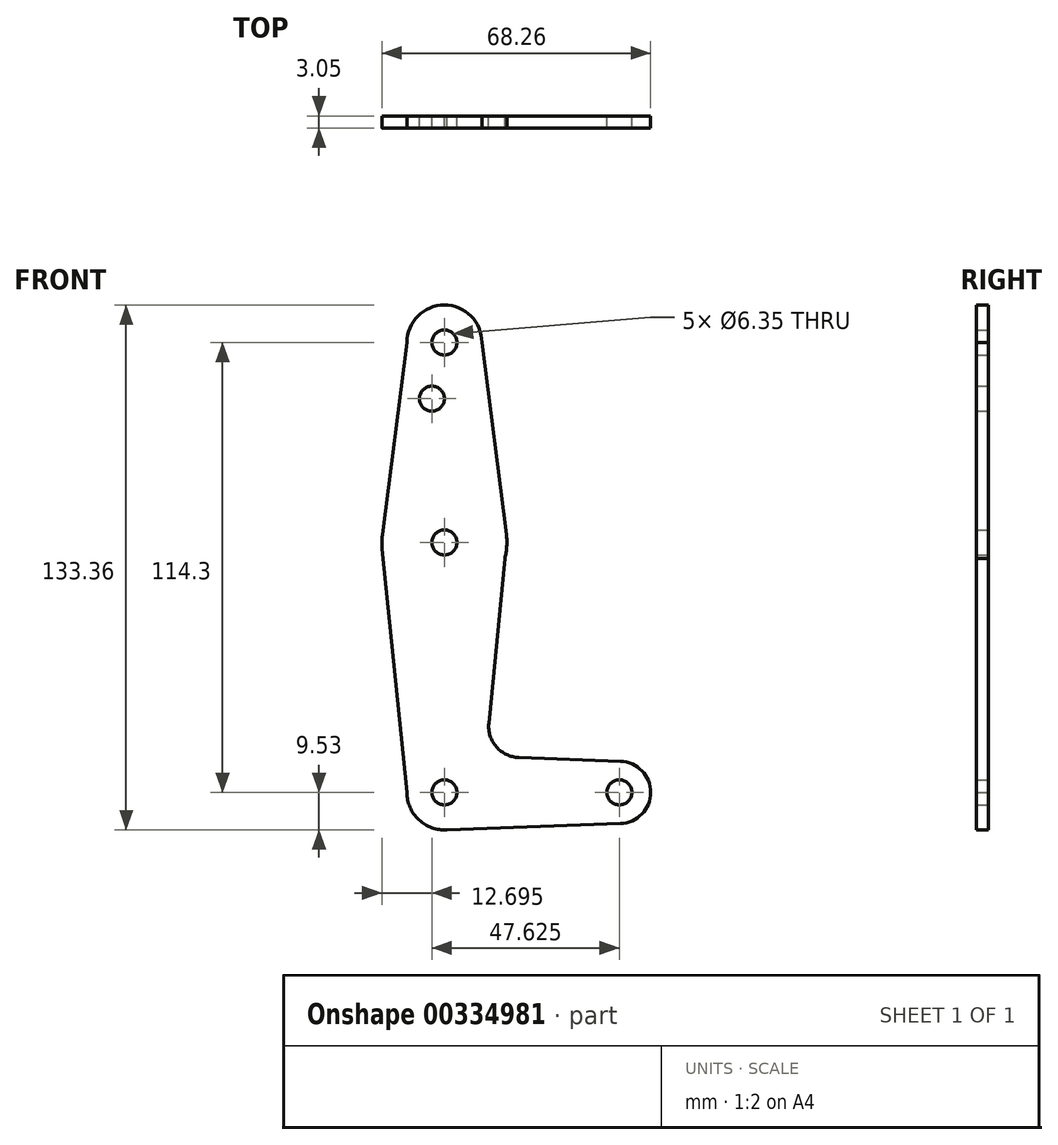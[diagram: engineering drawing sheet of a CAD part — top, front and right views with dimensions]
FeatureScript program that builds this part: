
annotation { "Feature Type Name" : "Feature", "Feature Type Description" : "" }
export const myFeature = defineFeature(function(context is Context, id is Id, definition is map)
    precondition{}
    {
        {
            var Q0;
            Q0=qCreatedBy(makeId("Front.planeOp"),FACE);
            var sketch = newSketch(context, id + "F0", { "sketchPlane" : qUnion([Q0])});
            skLineSegment(sketch, "E0", {"start": v(0, 0) * mm, "end": v(0, 63.5) * mm, "construction": true});
            skLineSegment(sketch, "E1", {"start": v(0, 0) * mm, "end": v(44.45, 0) * mm, "construction": true});
            skLineSegment(sketch, "E2", {"start": v(0, 63.5) * mm, "end": v(0, 114.3) * mm, "construction": true});
            skCircle(sketch, "E3", {"center": v(0, 114.3) * mm, "radius": 9.53 * mm});
            skCircle(sketch, "E4", {"center": v(0, 63.5) * mm, "radius": 15.88 * mm});
            skCircle(sketch, "E5", {"center": v(0, 0) * mm, "radius": 9.53 * mm});
            skCircle(sketch, "E6", {"center": v(44.45, 0) * mm, "radius": 7.94 * mm});
            skLineSegment(sketch, "E7", {"start": v(-9.53, 114.3) * mm, "end": v(-15.75, 65.5) * mm});
            skLineSegment(sketch, "E8", {"start": v(9.53, 114.3) * mm, "end": v(15.75, 65.5) * mm});
            skLineSegment(sketch, "E9", {"start": v(15.75, 63.5) * mm, "end": v(11.28, 17.57) * mm});
            skLineSegment(sketch, "E10", {"start": v(18.9, 8.85) * mm, "end": v(44.73, 7.93) * mm});
            skLineSegment(sketch, "E11", {"start": v(0, -9.53) * mm, "end": v(44.73, -7.93) * mm});
            skCircle(sketch, "E12", {"center": v(0, 114.3) * mm, "radius": 3.18 * mm});
            skCircle(sketch, "E13", {"center": v(-3.18, 100.03) * mm, "radius": 3.18 * mm});
            skCircle(sketch, "E14", {"center": v(0, 63.5) * mm, "radius": 3.18 * mm});
            skCircle(sketch, "E15", {"center": v(0, 0) * mm, "radius": 3.18 * mm});
            skCircle(sketch, "E16", {"center": v(44.45, 0) * mm, "radius": 3.18 * mm});
            skArc(sketch, "E17.filletArc", {"start": v(11.28, 17.57) * mm, "mid": v(13.21, 11.56) * mm, "end": v(18.9, 8.85) * mm});
            skLineSegment(sketch, "E18", {"start": v(-9.53, 0) * mm, "end": v(-15.8, 61.9) * mm});
            skSolve(sketch);
        }
        {
            var Q0;
            Q0 = qSketchRegion(id + "F0", true);
            extrude(context, id + "F1", {"entities" : qUnion([Q0]), "depth" : 3.05 * mm});
        }
    });
